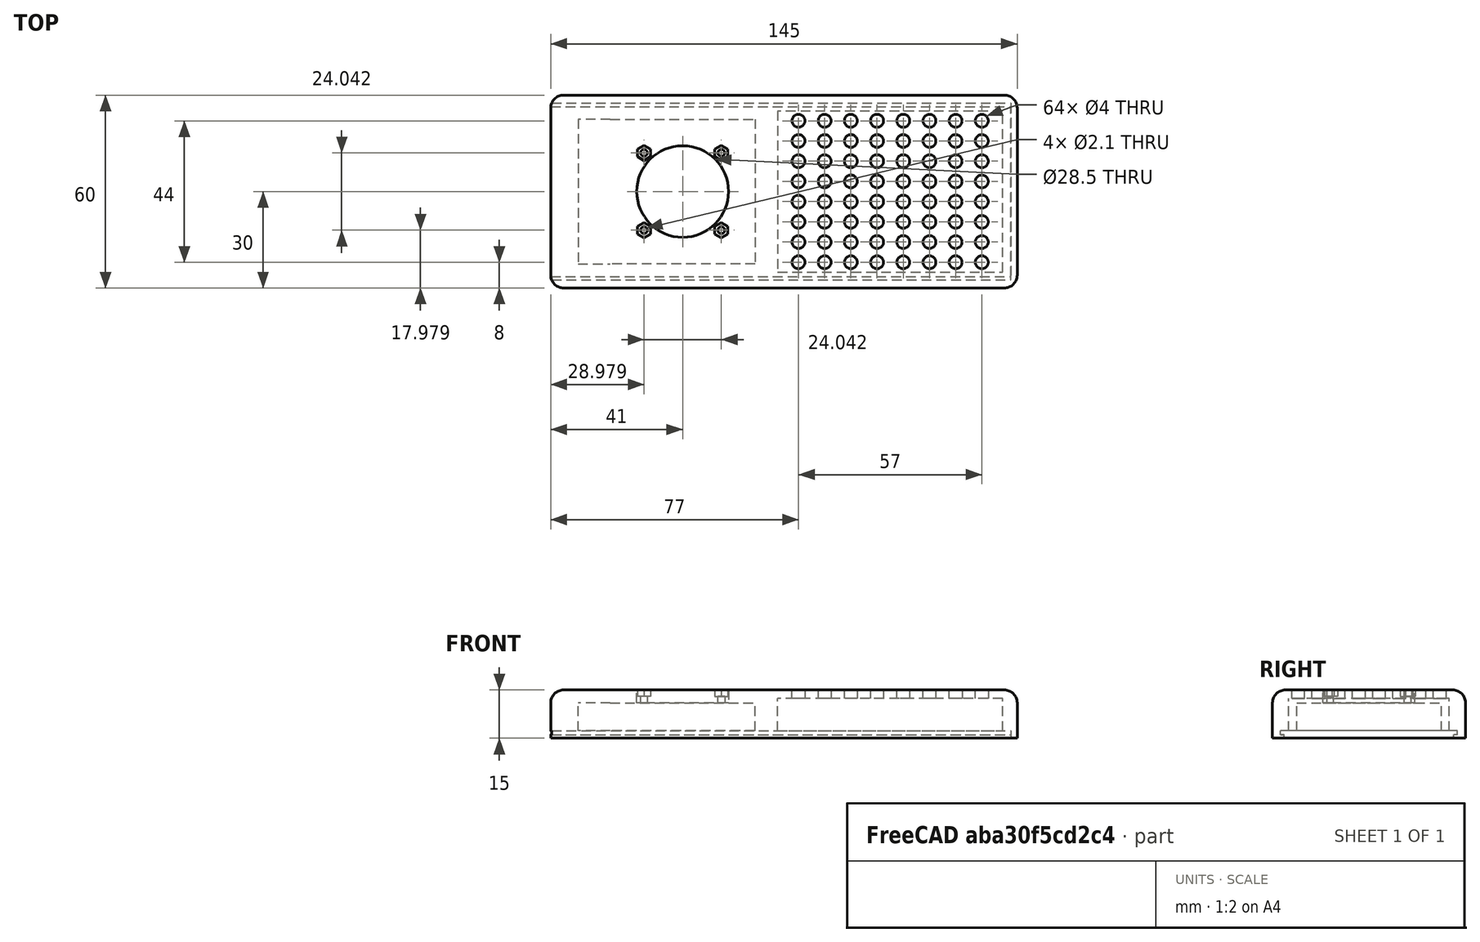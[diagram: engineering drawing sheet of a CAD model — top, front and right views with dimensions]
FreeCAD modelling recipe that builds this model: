
FCSTD DOCUMENT  (FreeCAD 0.21R33771 (Git))
Label: ESP_LID_CHAMBERS
License: All rights reserved
LicenseURL: https://en.wikipedia.org/wiki/All_rights_reserved
objects: Sketcher::SketchObject×8, PartDesign::Pocket×7, PartDesign::LinearPattern×2, PartDesign::Pad×1, PartDesign::Fillet×1, PartDesign::Body×1, Mesh::Feature×1
note: 29 computed .brp shape members not serialized (recipe doc carries the construction recipe); baked Part::Feature solids carry a one-line shape summary decoded from their .brp

FEATURE [Sketcher::SketchObject] Sketch
  FullyConstrained = true
  MapMode = 5
  Support = -> [XY_Plane]
  sketch-geometry (7):
    g0: LineSegment StartX=-72.5 StartY=30 StartZ=0 EndX=72.5 EndY=30 EndZ=0
    g1: LineSegment StartX=72.5 StartY=30 StartZ=0 EndX=72.5 EndY=-30 EndZ=0
    g2: LineSegment StartX=72.5 StartY=-30 StartZ=0 EndX=-72.5 EndY=-30 EndZ=0
    g3: LineSegment StartX=-72.5 StartY=-30 StartZ=0 EndX=-72.5 EndY=30 EndZ=0
    g4: LineSegment StartX=-72.5 StartY=30 StartZ=0 EndX=0 EndY=0 EndZ=0
    g5: LineSegment StartX=0 StartY=0 StartZ=0 EndX=72.5 EndY=-30 EndZ=0
    g6: LineSegment StartX=72.5 StartY=30 StartZ=0 EndX=0 EndY=0 EndZ=0
  constraints (18):
    c: Coincident(g0,g1)
    c: Coincident(g1,g2)
    c: Coincident(g2,g3)
    c: Coincident(g3,g0)
    c: Horizontal(g0)
    c: Horizontal(g2)
    c: Vertical(g1)
    c: Vertical(g3)
    c: Distance(g0) = 145
    c: Distance(g1) = 60
    c: Coincident(g4,g0)
    c: Coincident(g4,g-1)
    c: Coincident(g5,g4)
    c: Coincident(g5,g1)
    c: Coincident(g6,g0)
    c: Coincident(g6,g4)
    c: Equal(g6,g4)
    c: Equal(g6,g5)
FEATURE [Sketcher::SketchObject] Sketch003
  FullyConstrained = false
  MapMode = 5
  Placement = pos=(0,0,15) rot=(0,0,1;0rad)
  sketch-geometry (2):
    g0: LineSegment StartX=-68.5 StartY=0 StartZ=0 EndX=-31.5 EndY=0 EndZ=0
    g1: Circle CenterX=-31.5 CenterY=0 CenterZ=0 NormalX=0 NormalY=0 NormalZ=1 AngleXU=0 Radius=14.25
  constraints (5):
    c: PointOnObject(g0,g-1)
    c: Horizontal(g0)
    c: Distance(g0) = 37
    c: Coincident(g1,g0)
    c: Diameter(g1) = 28.5
FEATURE [Sketcher::SketchObject] Sketch004
  FullyConstrained = false
  MapMode = 5
  Placement = pos=(0,0,0) rot=(1,0,0;3.14159rad)
  sketch-geometry (10):
    g0: LineSegment StartX=-72.5 StartY=0 StartZ=0 EndX=-31.5 EndY=0 EndZ=0
    g1: LineSegment StartX=-54 StartY=22.5 StartZ=0 EndX=-9 EndY=22.5 EndZ=0
    g2: LineSegment StartX=-9 StartY=22.5 StartZ=0 EndX=-9 EndY=-22.5 EndZ=0
    g3: LineSegment StartX=-9 StartY=-22.5 StartZ=0 EndX=-54 EndY=-22.5 EndZ=0
    g4: LineSegment StartX=-54 StartY=22.5 StartZ=0 EndX=-31.5 EndY=0 EndZ=0
    g5: LineSegment StartX=-31.5 StartY=0 StartZ=0 EndX=-9 EndY=22.5 EndZ=0
    g6: LineSegment StartX=-31.5 StartY=0 StartZ=0 EndX=-9 EndY=-22.5 EndZ=0
    g7: LineSegment StartX=-54 StartY=22.5 StartZ=0 EndX=-64 EndY=22.5 EndZ=0
    g8: LineSegment StartX=-64 StartY=22.5 StartZ=0 EndX=-64 EndY=-22.5 EndZ=0
    g9: LineSegment StartX=-64 StartY=-22.5 StartZ=0 EndX=-54 EndY=-22.5 EndZ=0
  constraints (28):
    c: PointOnObject(g0,g-1)
    c: Horizontal(g0)
    c: Distance(g0) = 41
    c: Coincident(g1,g2)
    c: Coincident(g2,g3)
    c: Horizontal(g1)
    c: Horizontal(g3)
    c: Vertical(g2)
    c: Equal(g1,g2)
    c: Distance(g1) = 45
    c: Coincident(g4,g1)
    c: Coincident(g4,g0)
    c: Coincident(g5,g0)
    c: Coincident(g5,g1)
    c: Coincident(g6,g0)
    c: Coincident(g6,g2)
    c: Equal(g5,g4)
    c: Equal(g6,g5)
    c: Coincident(g7,g8)
    c: Coincident(g8,g9)
    c: Horizontal(g7)
    c: Horizontal(g9)
    c: Vertical(g8)
    c: Coincident(g7,g1)
    c: PointOnObject(g9,g3)
    c: Distance(g7) = 10
    c: Equal(g1,g3)
    c: Equal(g7,g9)
FEATURE [PartDesign::Pad] Pad
  Direction = (0,0,1)
  Length = 15
  Length2 = 10
  Profile = -> Sketch
  ReferenceAxis = -> Sketch [N_Axis]
  Type = 0
FEATURE [PartDesign::Fillet] Fillet
  Base = -> Pad [Edge4,Edge2,Edge1,Edge12,Edge8,Edge10,Edge5,Edge7]
  BaseFeature = -> Pad
  Radius = 4
  SupportTransform = false
  UseAllEdges = false
FEATURE [PartDesign::Pocket] Pocket002
  BaseFeature = -> Fillet
  Direction = (0,0,-1)
  Length = 5
  Length2 = 5
  Profile = -> Sketch003
  ReferenceAxis = -> Sketch003 [N_Axis]
  Type = 1
FEATURE [Sketcher::SketchObject] Sketch001
  ExternalGeometry = -> [Pocket002]
  FullyConstrained = true
  MapMode = 5
  Placement = pos=(0,0,15) rot=(0,0,1;0rad)
  sketch-geometry (39):
    g0: LineSegment StartX=-68.5 StartY=0 StartZ=0 EndX=-31.5 EndY=0 EndZ=0
    g1: LineSegment StartX=-31.5 StartY=0 StartZ=0 EndX=-19.4792 EndY=12.0208 EndZ=0
    g2: LineSegment StartX=-17.444 StartY=10.8458 StartZ=0 EndX=-17.444 EndY=13.1958 EndZ=0
    g3: LineSegment StartX=-17.444 StartY=13.1958 StartZ=0 EndX=-19.4792 EndY=14.3708 EndZ=0
    g4: LineSegment StartX=-19.4792 StartY=14.3708 StartZ=0 EndX=-21.5143 EndY=13.1958 EndZ=0
    g5: LineSegment StartX=-21.5143 StartY=13.1958 StartZ=0 EndX=-21.5143 EndY=10.8458 EndZ=0
    g6: LineSegment StartX=-21.5143 StartY=10.8458 StartZ=0 EndX=-19.4792 EndY=9.67082 EndZ=0
    g7: LineSegment StartX=-19.4792 StartY=9.67082 StartZ=0 EndX=-17.444 EndY=10.8458 EndZ=0
    g8: Circle CenterX=-19.4792 CenterY=12.0208 CenterZ=0 NormalX=0 NormalY=0 NormalZ=1 AngleXU=0 Radius=2.35
    g9: LineSegment StartX=-31.5 StartY=0 StartZ=0 EndX=-43.5208 EndY=-12.0208 EndZ=0
    g10: LineSegment StartX=-31.5 StartY=0 StartZ=0 EndX=-43.5208 EndY=12.0208 EndZ=0
    g11: LineSegment StartX=-31.5 StartY=0 StartZ=0 EndX=-19.4792 EndY=-12.0208 EndZ=0
    g12: LineSegment StartX=-19.4792 StartY=-12.0208 StartZ=0 EndX=0 EndY=0 EndZ=0
    g13: LineSegment StartX=-19.4792 StartY=12.0208 StartZ=0 EndX=0 EndY=0 EndZ=0
    g14: LineSegment StartX=-19.4792 StartY=12.0208 StartZ=0 EndX=-19.4792 EndY=14.3708 EndZ=0
    g15: LineSegment StartX=-41.4857 StartY=13.1958 StartZ=0 EndX=-43.5208 EndY=14.3708 EndZ=0
    g16: LineSegment StartX=-43.5208 StartY=14.3708 StartZ=0 EndX=-45.556 EndY=13.1958 EndZ=0
    g17: LineSegment StartX=-45.556 StartY=13.1958 StartZ=0 EndX=-45.556 EndY=10.8458 EndZ=0
    g18: LineSegment StartX=-45.556 StartY=10.8458 StartZ=0 EndX=-43.5208 EndY=9.67082 EndZ=0
    g19: LineSegment StartX=-43.5208 StartY=9.67082 StartZ=0 EndX=-41.4857 EndY=10.8458 EndZ=0
    g20: LineSegment StartX=-41.4857 StartY=10.8458 StartZ=0 EndX=-41.4857 EndY=13.1958 EndZ=0
    g21: Circle CenterX=-43.5208 CenterY=12.0208 CenterZ=0 NormalX=0 NormalY=0 NormalZ=1 AngleXU=0 Radius=2.35
    g22: LineSegment StartX=-45.556 StartY=-10.8458 StartZ=0 EndX=-45.556 EndY=-13.1958 EndZ=0
    g23: LineSegment StartX=-45.556 StartY=-13.1958 StartZ=0 EndX=-43.5208 EndY=-14.3708 EndZ=0
    g24: LineSegment StartX=-43.5208 StartY=-14.3708 StartZ=0 EndX=-41.4857 EndY=-13.1958 EndZ=0
    g25: LineSegment StartX=-41.4857 StartY=-13.1958 StartZ=0 EndX=-41.4857 EndY=-10.8458 EndZ=0
    g26: LineSegment StartX=-41.4857 StartY=-10.8458 StartZ=0 EndX=-43.5208 EndY=-9.67082 EndZ=0
    g27: LineSegment StartX=-43.5208 StartY=-9.67082 StartZ=0 EndX=-45.556 EndY=-10.8458 EndZ=0
    g28: Circle CenterX=-43.5208 CenterY=-12.0208 CenterZ=0 NormalX=0 NormalY=0 NormalZ=1 AngleXU=0 Radius=2.35
    g29: LineSegment StartX=-17.444 StartY=-13.1958 StartZ=0 EndX=-17.444 EndY=-10.8458 EndZ=0
    g30: LineSegment StartX=-17.444 StartY=-10.8458 StartZ=0 EndX=-19.4792 EndY=-9.67082 EndZ=0
    g31: LineSegment StartX=-19.4792 StartY=-9.67082 StartZ=0 EndX=-21.5143 EndY=-10.8458 EndZ=0
    g32: LineSegment StartX=-21.5143 StartY=-10.8458 StartZ=0 EndX=-21.5143 EndY=-13.1958 EndZ=0
    g33: LineSegment StartX=-21.5143 StartY=-13.1958 StartZ=0 EndX=-19.4792 EndY=-14.3708 EndZ=0
    g34: LineSegment StartX=-19.4792 StartY=-14.3708 StartZ=0 EndX=-17.444 EndY=-13.1958 EndZ=0
    g35: Circle CenterX=-19.4792 CenterY=-12.0208 CenterZ=0 NormalX=0 NormalY=0 NormalZ=1 AngleXU=0 Radius=2.35
    g36: LineSegment StartX=-43.5208 StartY=14.3708 StartZ=0 EndX=-43.5208 EndY=12.0208 EndZ=0
    g37: LineSegment StartX=-43.5208 StartY=-9.67082 StartZ=0 EndX=-43.5208 EndY=-12.0208 EndZ=0
    g38: LineSegment StartX=-19.4792 StartY=-9.67082 StartZ=0 EndX=-19.4792 EndY=-12.0208 EndZ=0
  constraints (92):
    c: Horizontal(g0)
    c: Distance(g0) = 37
    c: Coincident(g1,g0)
    c: Distance(g1) = 17
    c: Coincident(g2,g3)
    c: Coincident(g3,g4)
    c: Coincident(g4,g5)
    c: Coincident(g5,g6)
    c: Coincident(g6,g7)
    c: Coincident(g7,g2)
    c: Equal(g2, g3-g7) x5
    c: PointOnObject(g2,g8)
    c: PointOnObject(g3,g8)
    c: PointOnObject(g4,g8)
    c: PointOnObject(g5,g8)
    c: PointOnObject(g6,g8)
    c: PointOnObject(g7,g8)
    c: Coincident(g8,g1)
    c: Diameter(g8) = 4.7
    c: Coincident(g9,g0)
    c: Coincident(g10,g0)
    c: Coincident(g11,g0)
    c: Coincident(g12,g11)
    c: Coincident(g12,g-1)
    c: Coincident(g13,g1)
    c: Coincident(g13,g12)
    c: Equal(g13,g12)
    c: Equal(g1,g9)
    c: Equal(g10,g11)
    c: Equal(g11,g1)
    c: Perpendicular(g11,g1)
    c: Perpendicular(g11,g9)
    c: Perpendicular(g9,g10)
    c: Coincident(g14,g1)
    c: Coincident(g14,g3)
    c: Vertical(g14)
    c: Coincident(g15,g16)
    c: Coincident(g16,g17)
    c: Coincident(g17,g18)
    c: Coincident(g18,g19)
    c: Coincident(g19,g20)
    c: Coincident(g20,g15)
    c: Equal(g15, g16-g20) x5
    c: PointOnObject(g15,g21)
    c: PointOnObject(g16,g21)
    c: PointOnObject(g17,g21)
    c: PointOnObject(g18,g21)
    c: PointOnObject(g19,g21)
    c: PointOnObject(g20,g21)
    c: Coincident(g21,g10)
    c: Coincident(g22,g23)
    c: Coincident(g23,g24)
    c: Coincident(g24,g25)
    c: Coincident(g25,g26)
    c: Coincident(g26,g27)
    c: Coincident(g27,g22)
    c: Equal(g22, g23-g27) x5
    c: PointOnObject(g22,g28)
    c: PointOnObject(g23,g28)
    c: PointOnObject(g24,g28)
    c: PointOnObject(g25,g28)
    c: PointOnObject(g26,g28)
    c: PointOnObject(g27,g28)
    c: Coincident(g28,g9)
    c: Coincident(g29,g30)
    c: Coincident(g30,g31)
    c: Coincident(g31,g32)
    c: Coincident(g32,g33)
    c: Coincident(g33,g34)
    c: Coincident(g34,g29)
    c: Equal(g29, g30-g34) x5
    c: PointOnObject(g29,g35)
    c: PointOnObject(g30,g35)
    c: PointOnObject(g31,g35)
    c: PointOnObject(g32,g35)
    c: PointOnObject(g33,g35)
    c: PointOnObject(g34,g35)
    c: Coincident(g35,g11)
    c: Equal(g8,g35)
    c: Equal(g28,g8)
    c: Equal(g21,g8)
    c: Coincident(g36,g15)
    c: Coincident(g36,g10)
    c: Coincident(g37,g26)
    c: Coincident(g37,g9)
    c: Coincident(g38,g30)
    c: Coincident(g38,g11)
    c: Vertical(g38)
    c: Vertical(g37)
    c: Vertical(g36)
    c: PointOnObject(g0,g-3)
    c: PointOnObject(g0,g-1)
FEATURE [PartDesign::Pocket] Pocket
  BaseFeature = -> Pocket002
  Direction = (0,0,-1)
  Length = 2
  Length2 = 5
  Profile = -> Sketch001
  ReferenceAxis = -> Sketch001 [N_Axis]
  Type = 0
FEATURE [Sketcher::SketchObject] Sketch002
  ExternalGeometry = -> [Pocket]
  FullyConstrained = true
  MapMode = 5
  Placement = pos=(0,0,15) rot=(0,0,1;0rad)
  sketch-geometry (11):
    g0: LineSegment StartX=-68.5 StartY=0 StartZ=0 EndX=-31.5 EndY=0 EndZ=0
    g1: LineSegment StartX=-31.5 StartY=0 StartZ=0 EndX=-19.4792 EndY=12.0208 EndZ=0
    g2: LineSegment StartX=-19.4792 StartY=12.0208 StartZ=0 EndX=0 EndY=0 EndZ=0
    g3: LineSegment StartX=0 StartY=0 StartZ=0 EndX=-19.4792 EndY=-12.0208 EndZ=0
    g4: LineSegment StartX=-19.4792 StartY=-12.0208 StartZ=0 EndX=-31.5 EndY=0 EndZ=0
    g5: LineSegment StartX=-31.5 StartY=0 StartZ=0 EndX=-43.5208 EndY=-12.0208 EndZ=0
    g6: LineSegment StartX=-31.5 StartY=0 StartZ=0 EndX=-43.5208 EndY=12.0208 EndZ=0
    g7: Circle CenterX=-19.4792 CenterY=12.0208 CenterZ=0 NormalX=0 NormalY=0 NormalZ=1 AngleXU=0 Radius=1.05
    g8: Circle CenterX=-43.5208 CenterY=12.0208 CenterZ=0 NormalX=0 NormalY=0 NormalZ=1 AngleXU=0 Radius=1.05
    g9: Circle CenterX=-43.5208 CenterY=-12.0208 CenterZ=0 NormalX=0 NormalY=0 NormalZ=1 AngleXU=0 Radius=1.05
    g10: Circle CenterX=-19.4792 CenterY=-12.0208 CenterZ=0 NormalX=0 NormalY=0 NormalZ=1 AngleXU=0 Radius=1.05
  constraints (28):
    c: PointOnObject(g0,g-1)
    c: PointOnObject(g0,g-1)
    c: Distance(g0) = 37
    c: Coincident(g1,g0)
    c: Coincident(g2,g1)
    c: Coincident(g2,g-1)
    c: Coincident(g3,g2)
    c: Coincident(g4,g3)
    c: Coincident(g4,g0)
    c: Coincident(g5,g0)
    c: Coincident(g6,g0)
    c: Equal(g2,g3)
    c: Equal(g1,g4)
    c: Equal(g4,g5)
    c: Equal(g5,g6)
    c: Perpendicular(g5,g6)
    c: Perpendicular(g5,g4)
    c: Perpendicular(g1,g4)
    c: Distance(g1) = 17
    c: Coincident(g7,g1)
    c: Coincident(g8,g6)
    c: Coincident(g9,g5)
    c: Coincident(g10,g3)
    c: Diameter(g7) = 2.1
    c: Equal(g7,g10)
    c: Equal(g10,g9)
    c: Equal(g9,g8)
    c: PointOnObject(g0,g-3)
FEATURE [PartDesign::Pocket] Pocket003
  BaseFeature = -> Pocket
  Direction = (0,0,-1)
  Length = 5
  Length2 = 5
  Profile = -> Sketch002
  ReferenceAxis = -> Sketch002 [N_Axis]
  Type = 1
FEATURE [PartDesign::Pocket] Pocket004
  BaseFeature = -> Pocket003
  Direction = (0,0,1)
  Length = 11
  Length2 = 5
  Profile = -> Sketch004
  ReferenceAxis = -> Sketch004 [N_Axis]
  Type = 0
FEATURE [Sketcher::SketchObject] Sketch007
  FullyConstrained = true
  MapMode = 5
  Placement = pos=(-72.5,0,0) rot=(0.57735,-0.57735,-0.57735;2.0944rad)
  Support = -> [Pocket004]
  sketch-geometry (10):
    g0: LineSegment StartX=-27.5 StartY=2.3 StartZ=0 EndX=27.5 EndY=2.3 EndZ=0
    g1: LineSegment StartX=-27.5 StartY=2.3 StartZ=0 EndX=-27.5 EndY=1.1 EndZ=0
    g2: LineSegment StartX=-27.5 StartY=1.1 StartZ=0 EndX=-26.4 EndY=1.1 EndZ=0
    g3: LineSegment StartX=-26.4 StartY=1.1 StartZ=0 EndX=-26.4 EndY=0 EndZ=0
    g4: LineSegment StartX=27.5 StartY=2.3 StartZ=0 EndX=27.5 EndY=1.1 EndZ=0
    g5: LineSegment StartX=27.5 StartY=1.1 StartZ=0 EndX=26.4 EndY=1.1 EndZ=0
    g6: LineSegment StartX=26.4 StartY=1.1 StartZ=0 EndX=26.4 EndY=0 EndZ=0
    g7: LineSegment StartX=26.4 StartY=0 StartZ=0 EndX=-26.4 EndY=0 EndZ=0
    g8: LineSegment StartX=-27.5 StartY=2.3 StartZ=0 EndX=0 EndY=0 EndZ=0
    g9: LineSegment StartX=0 StartY=0 StartZ=0 EndX=27.5 EndY=2.3 EndZ=0
  constraints (28):
    c: Horizontal(g0)
    c: Distance(g0) = 55
    c: Coincident(g1,g0)
    c: Vertical(g1)
    c: Coincident(g2,g1)
    c: Horizontal(g2)
    c: Coincident(g3,g2)
    c: PointOnObject(g3,g-1)
    c: Vertical(g3)
    c: Coincident(g4,g0)
    c: Vertical(g4)
    c: Coincident(g5,g4)
    c: Horizontal(g5)
    c: Coincident(g6,g5)
    c: PointOnObject(g6,g-1)
    c: Vertical(g6)
    c: Coincident(g7,g6)
    c: Coincident(g7,g3)
    c: Distance(g1) = 1.2
    c: Distance(g2) = 1.1
    c: Distance(g3) = 1.1
    c: Equal(g1,g4)
    c: Equal(g5,g2)
    c: Coincident(g8,g0)
    c: Coincident(g8,g-1)
    c: Coincident(g9,g8)
    c: Coincident(g9,g0)
    c: Equal(g8,g9)
FEATURE [PartDesign::Pocket] Pocket005
  BaseFeature = -> Pocket004
  Direction = (1,0,0)
  Length = 143
  Length2 = 5
  Profile = -> Sketch007
  ReferenceAxis = -> Sketch007 [N_Axis]
  Type = 0
FEATURE [Sketcher::SketchObject] Sketch008
  FullyConstrained = true
  MapMode = 5
  Placement = pos=(0,0,2.3) rot=(1,0,0;3.14159rad)
  Support = -> [Pocket005]
  sketch-geometry (8):
    g0: LineSegment StartX=0 StartY=0 StartZ=0 EndX=-2 EndY=0 EndZ=0
    g1: LineSegment StartX=-2 StartY=0 StartZ=0 EndX=-2 EndY=25 EndZ=0
    g2: LineSegment StartX=-2 StartY=0 StartZ=0 EndX=-2 EndY=-25 EndZ=0
    g3: LineSegment StartX=-2 StartY=-25 StartZ=0 EndX=68 EndY=-25 EndZ=0
    g4: LineSegment StartX=-2 StartY=25 StartZ=0 EndX=68 EndY=25 EndZ=0
    g5: LineSegment StartX=68 StartY=25 StartZ=0 EndX=68 EndY=-25 EndZ=0
    g6: LineSegment StartX=68 StartY=-25 StartZ=0 EndX=-2 EndY=-25 EndZ=0
    g7: LineSegment StartX=-2 StartY=-25 StartZ=0 EndX=-2 EndY=25 EndZ=0
  constraints (22):
    c: Coincident(g0,g-1)
    c: PointOnObject(g0,g-1)
    c: Distance(g0) = 2
    c: Coincident(g1,g0)
    c: Vertical(g1)
    c: Coincident(g2,g0)
    c: Vertical(g2)
    c: Distance(g1) = 25
    c: Equal(g1,g2)
    c: Coincident(g3,g2)
    c: Horizontal(g3)
    c: Distance(g3) = 70
    c: Coincident(g4,g5)
    c: Coincident(g5,g6)
    c: Coincident(g6,g7)
    c: Coincident(g7,g4)
    c: Horizontal(g4)
    c: Horizontal(g6)
    c: Vertical(g5)
    c: Vertical(g7)
    c: Coincident(g4,g1)
    c: Coincident(g5,g3)
FEATURE [PartDesign::Pocket] Pocket006
  BaseFeature = -> Pocket005
  Direction = (0,0,1)
  Length = 10
  Length2 = 5
  Profile = -> Sketch008
  ReferenceAxis = -> Sketch008 [N_Axis]
  Type = 0
FEATURE [Sketcher::SketchObject] Sketch006
  ExternalGeometry = -> [Pocket006]
  FullyConstrained = true
  MapMode = 5
  Placement = pos=(0,0,15) rot=(0,0,1;0rad)
  sketch-geometry (18):
    g0: Circle CenterX=61.5 CenterY=-3.14286 CenterZ=0 NormalX=0 NormalY=0 NormalZ=1 AngleXU=0 Radius=2
    g1: Circle CenterX=61.5 CenterY=3.14286 CenterZ=0 NormalX=0 NormalY=0 NormalZ=1 AngleXU=0 Radius=2
    g2: Circle CenterX=61.5 CenterY=9.42857 CenterZ=0 NormalX=0 NormalY=0 NormalZ=1 AngleXU=0 Radius=2
    g3: Circle CenterX=61.5 CenterY=15.7143 CenterZ=0 NormalX=0 NormalY=0 NormalZ=1 AngleXU=0 Radius=2
    g4: Circle CenterX=61.5 CenterY=22 CenterZ=0 NormalX=0 NormalY=0 NormalZ=1 AngleXU=0 Radius=2
    g5: Circle CenterX=61.5 CenterY=-22 CenterZ=0 NormalX=0 NormalY=0 NormalZ=1 AngleXU=0 Radius=2
    g6: LineSegment StartX=61.5 StartY=22 StartZ=0 EndX=61.5 EndY=26 EndZ=0
    g7: LineSegment StartX=61.5 StartY=22 StartZ=0 EndX=68.5 EndY=22 EndZ=0
    g8: LineSegment StartX=61.5 StartY=22 StartZ=0 EndX=61.5 EndY=15.7143 EndZ=0
    g9: LineSegment StartX=61.5 StartY=15.7143 StartZ=0 EndX=61.5 EndY=9.42857 EndZ=0
    g10: LineSegment StartX=61.5 StartY=9.42857 StartZ=0 EndX=61.5 EndY=3.14286 EndZ=0
    g11: LineSegment StartX=61.5 StartY=3.14286 StartZ=0 EndX=61.5 EndY=-3.14286 EndZ=0
    g12: Circle CenterX=61.5 CenterY=-9.42857 CenterZ=0 NormalX=0 NormalY=0 NormalZ=1 AngleXU=0 Radius=2
    g13: Circle CenterX=61.5 CenterY=-15.7143 CenterZ=0 NormalX=0 NormalY=0 NormalZ=1 AngleXU=0 Radius=2
    g14: LineSegment StartX=61.5 StartY=-3.14286 StartZ=0 EndX=61.5 EndY=-9.42857 EndZ=0
    g15: LineSegment StartX=61.5 StartY=-9.42857 StartZ=0 EndX=61.5 EndY=-15.7143 EndZ=0
    g16: LineSegment StartX=61.5 StartY=-15.7143 StartZ=0 EndX=61.5 EndY=-22 EndZ=0
    g17: LineSegment StartX=61.5 StartY=-22 StartZ=0 EndX=61.5 EndY=-26 EndZ=0
  constraints (47):
    c: Coincident(g6,g4)
    c: PointOnObject(g6,g-3)
    c: Vertical(g6)
    c: Coincident(g7,g4)
    c: PointOnObject(g7,g-4)
    c: Horizontal(g7)
    c: Distance(g7) = 7
    c: Distance(g6) = 4
    c: Coincident(g8,g4)
    c: Coincident(g8,g3)
    c: Coincident(g9,g3)
    c: Coincident(g9,g2)
    c: Vertical(g9)
    c: Coincident(g10,g2)
    c: Coincident(g10,g1)
    c: Vertical(g10)
    c: Coincident(g11,g1)
    c: Coincident(g11,g0)
    c: Vertical(g11)
    c: Vertical(g8)
    c: Coincident(g14,g0)
    c: Coincident(g14,g12)
    c: Coincident(g15,g12)
    c: Coincident(g15,g13)
    c: Vertical(g15)
    c: Coincident(g16,g13)
    c: Coincident(g16,g5)
    c: Vertical(g16)
    c: Coincident(g17,g5)
    c: PointOnObject(g17,g-5)
    c: Vertical(g17)
    c: Equal(g6,g17)
    c: Equal(g16,g15)
    c: Equal(g14,g15)
    c: Equal(g14,g11)
    c: Equal(g11,g10)
    c: Equal(g10,g9)
    c: Equal(g9,g8)
    c: Diameter(g4) = 4
    c: Equal(g4,g3)
    c: Equal(g3,g2)
    c: Equal(g2,g1)
    c: Equal(g1,g0)
    c: Equal(g0,g12)
    c: Equal(g12,g13)
    c: Equal(g13,g5)
    c: Vertical(g14)
FEATURE [PartDesign::LinearPattern] LinearPattern
  Direction = -> Sketch006 [H_Axis]
  Length = 57
  Occurrences = 8
  Reversed = true
FEATURE [PartDesign::Pocket] Pocket007
  BaseFeature = -> Pocket006
  Direction = (0,0,-1)
  Length = 5
  Length2 = 5
  Profile = -> Sketch006
  ReferenceAxis = -> Sketch006 [N_Axis]
  Type = 1
FEATURE [PartDesign::LinearPattern] LinearPattern001
  BaseFeature = -> Pocket007
  Direction = -> Sketch006 [H_Axis]
  Length = 57
  Occurrences = 8
  Originals = -> [Pocket007]
  Reversed = true
FEATURE [PartDesign::Body] Body
  Group = -> [Sketch,Sketch001,Sketch002,Sketch003,Sketch004,Sketch006,LinearPattern,Pad,Fillet,Pocket002,Pocket,Pocket003,Pocket004,Sketch007,Pocket005,Sketch008,Pocket006,Pocket007,LinearPattern001]
  Origin = -> Origin
  Tip = -> LinearPattern001
FEATURE [Mesh::Feature] Mesh  label="Body (Meshed)"
